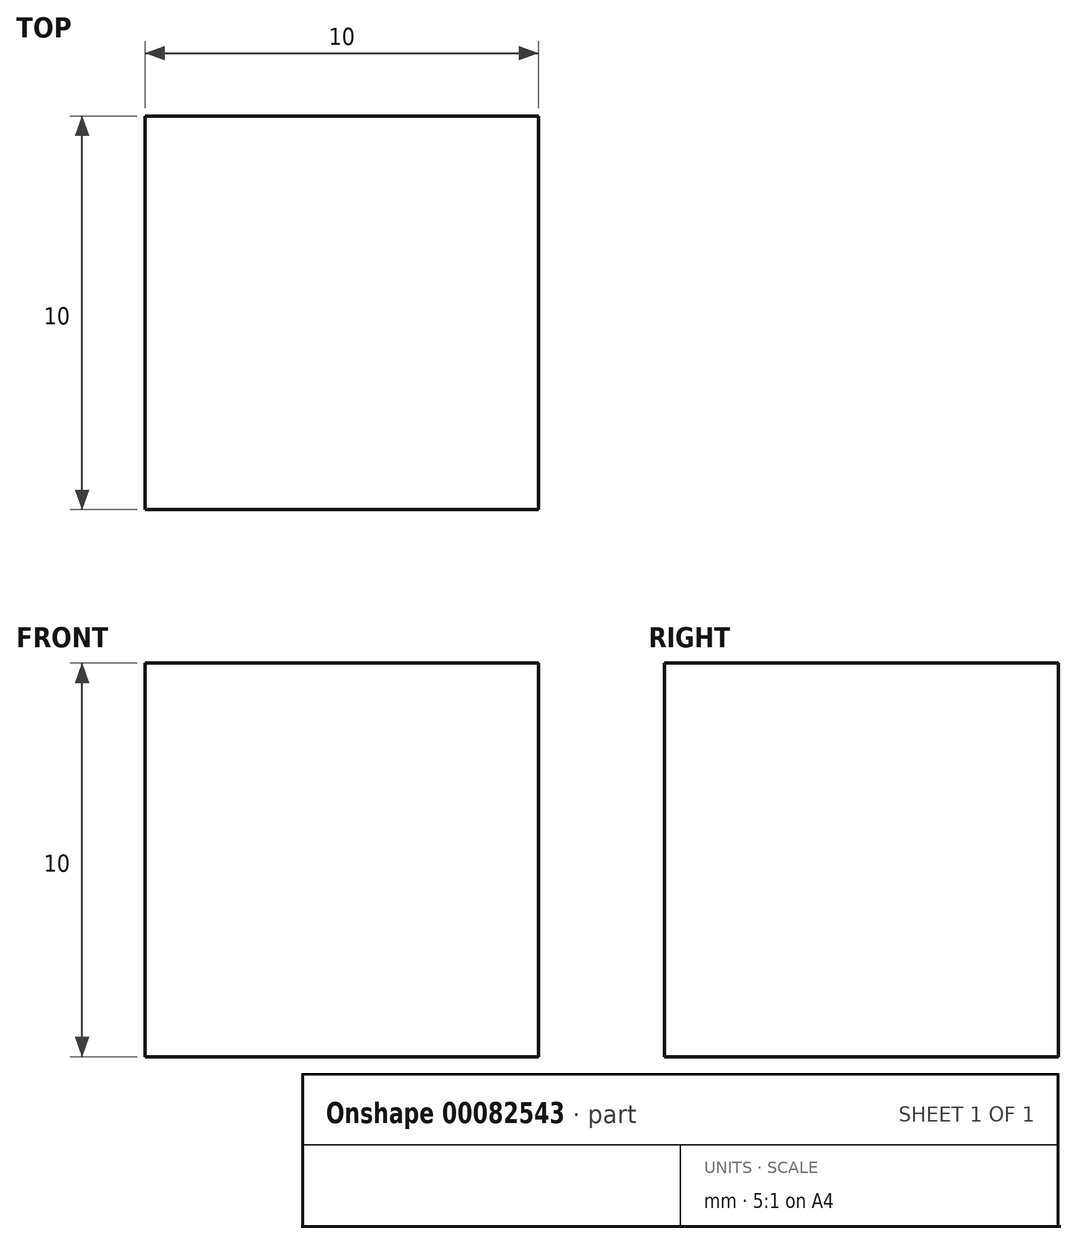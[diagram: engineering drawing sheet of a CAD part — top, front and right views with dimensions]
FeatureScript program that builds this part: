
annotation { "Feature Type Name" : "Feature", "Feature Type Description" : "" }
export const myFeature = defineFeature(function(context is Context, id is Id, definition is map)
    precondition{}
    {
        {
            var Q0;
            Q0=qCreatedBy(makeId("Front.planeOp"),FACE);
            var sketch = newSketch(context, id + "F0", { "sketchPlane" : qUnion([Q0])});
            skLineSegment(sketch, "E0.bottom", {"start": v(0, 0) * mm, "end": v(-10, 0) * mm});
            skLineSegment(sketch, "E0.top", {"start": v(0, 10) * mm, "end": v(-10, 10) * mm});
            skLineSegment(sketch, "E0.left", {"start": v(0, 0) * mm, "end": v(0, 10) * mm});
            skLineSegment(sketch, "E0.right", {"start": v(-10, 0) * mm, "end": v(-10, 10) * mm});
            skSolve(sketch);
        }
        {
            var Q0;
            Q0=makeQuery(id+"F0.imprint","IMPRINT",FACE,{"disambiguationData":[TD([[makeQuery(id+"F0.imprint","IMPRINT",EDGE,{"derivedFrom":sQuery(id+"F0.wireOp",EDGE,"E0.bottom")}),-1.0]])]});
            extrude(context, id + "F1", {"entities" : qUnion([Q0]), "depth" : 10 * mm});
        }
    });
